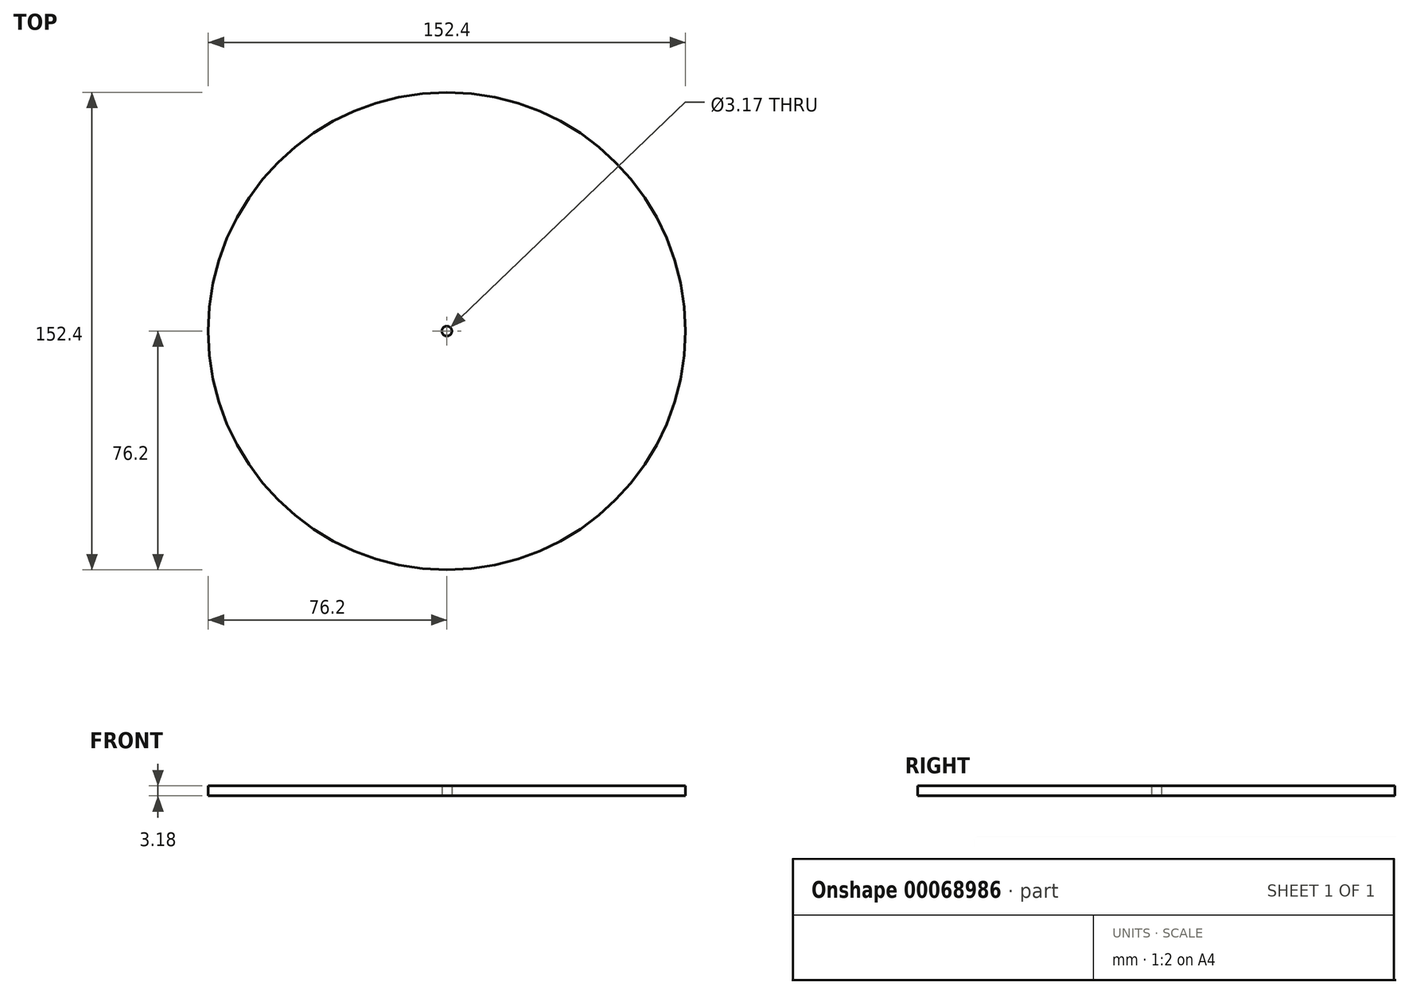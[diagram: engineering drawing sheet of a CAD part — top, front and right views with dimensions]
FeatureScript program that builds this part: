
annotation { "Feature Type Name" : "Feature", "Feature Type Description" : "" }
export const myFeature = defineFeature(function(context is Context, id is Id, definition is map)
    precondition{}
    {
        {
            var Q0;
            Q0=qCreatedBy(makeId("Top.planeOp"),FACE);
            var sketch = newSketch(context, id + "F0", { "sketchPlane" : qUnion([Q0])});
            skCircle(sketch, "E0", {"center": v(0, 0) * mm, "radius": 76.2 * mm});
            skCircle(sketch, "E1", {"center": v(0, 0) * mm, "radius": 1.59 * mm});
            skSolve(sketch);
        }
        {
            var Q0;
            Q0 = qSketchRegion(id + "F0", true);
            extrude(context, id + "F1", {"entities" : qUnion([Q0]), "depth" : 3.17 * mm});
        }
    });
